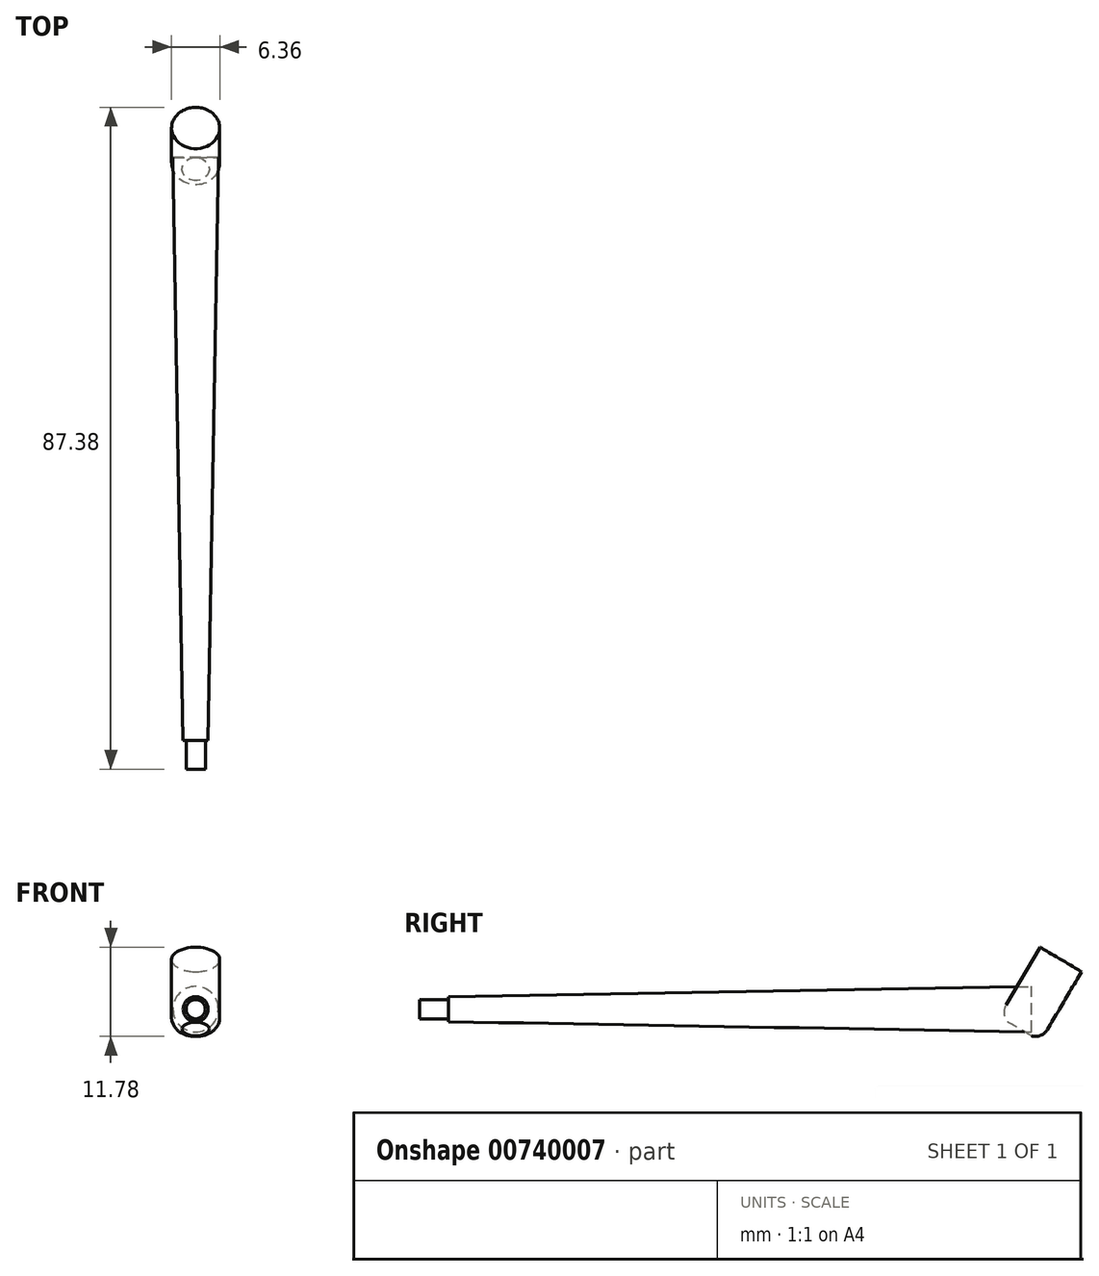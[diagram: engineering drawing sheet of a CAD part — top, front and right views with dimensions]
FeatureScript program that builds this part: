
annotation { "Feature Type Name" : "Feature", "Feature Type Description" : "" }
export const myFeature = defineFeature(function(context is Context, id is Id, definition is map)
    precondition{}
    {
        {
            var Q0;
            Q0=qCreatedBy(makeId("Front.planeOp"),FACE);
            var sketch = newSketch(context, id + "F0", { "sketchPlane" : qUnion([Q0])});
            skCircle(sketch, "E0", {"center": v(0, 0) * mm, "radius": 3 * mm});
            skSolve(sketch);
        }
        {
            var Q0;
            Q0=makeQuery(id+"F0.imprint","IMPRINT",FACE,{"disambiguationData":[TD([[makeQuery(id+"F0.imprint","IMPRINT",EDGE,{"derivedFrom":sQuery(id+"F0.wireOp",EDGE,"E0")}),1.0]])]});
            extrude(context, id + "F1", {"entities" : qUnion([Q0]), "depth" : 76.96 * mm, "offsetDistance" : 25.4 * mm, "hasDraft" : true, "draftAngle" : 1 * degree, "draftPullDirection" : true});
        }
        {
            var Q0;
            Q0=qCreatedBy(makeId("Right.planeOp"),FACE);
            var sketch = newSketch(context, id + "F2", { "sketchPlane" : qUnion([Q0])});
            skLineSegment(sketch, "E1", {"start": v(0, 0) * mm, "end": v(3.87, 6.56) * mm});
            skArc(sketch, "E2", {"start": v(0, -3.53) * mm, "mid": v(1.19, -3.47) * mm, "end": v(2.1, -2.7) * mm});
            skLineSegment(sketch, "E3", {"start": v(6.6, 4.95) * mm, "end": v(2.1, -2.7) * mm});
            skLineSegment(sketch, "E4", {"start": v(3.87, 6.56) * mm, "end": v(6.6, 4.95) * mm});
            skLineSegment(sketch, "E5", {"start": v(0.3, 0.5) * mm, "end": v(-1.54, -2.62) * mm});
            skLineSegment(sketch, "E6", {"start": v(0, -3.53) * mm, "end": v(-1.54, -2.62) * mm});
            skPoint(sketch, "E7.end.orphan", {"position": v(0, -2.62) * mm});
            skPoint(sketch, "E8.end.orphan", {"position": v(0, -3.3) * mm});
            skPoint(sketch, "E9.start.orphan", {"position": v(0, -0.2) * mm});
            skSolve(sketch);
        }
        {
            var Q0;
            Q0 = qSketchRegion(id + "F2", true);
            var Q1;
            Q1=sQuery(id+"F2.wireOp",EDGE,"E1");
            revolve(context, id + "F3", {"surfaceOperationType" : NewSurfaceOperationType.NEW, "entities" : qUnion([Q0]), "axis" : qUnion([Q1]), "revolveType" : RevolveType.ONE_DIRECTION, "angle" : 360 * degree});
        }
        {
            var Q0;
            Q0=makeQuery(id+"F1.opExtrude","CAP_FACE",FACE,{"disambiguationData":[OSD([sQuery(id+"F0.wireOp",EDGE,"E0")])],"isStart":false});
            var sketch = newSketch(context, id + "F4", { "sketchPlane" : qUnion([Q0])});
            skCircle(sketch, "E10", {"center": v(0, 0) * mm, "radius": 1.27 * mm});
            skSolve(sketch);
        }
        {
            var Q0;
            Q0=makeQuery(id+"F4.imprint","IMPRINT",FACE,{"disambiguationData":[TD([[makeQuery(id+"F4.imprint","IMPRINT",EDGE,{"derivedFrom":sQuery(id+"F4.wireOp",EDGE,"E10")}),1.0]])]});
            extrude(context, id + "F5", {"entities" : qUnion([Q0]), "operationType" : NewBodyOperationType.ADD, "depth" : 3.8 * mm, "offsetDistance" : 25.4 * mm});
        }
    });
